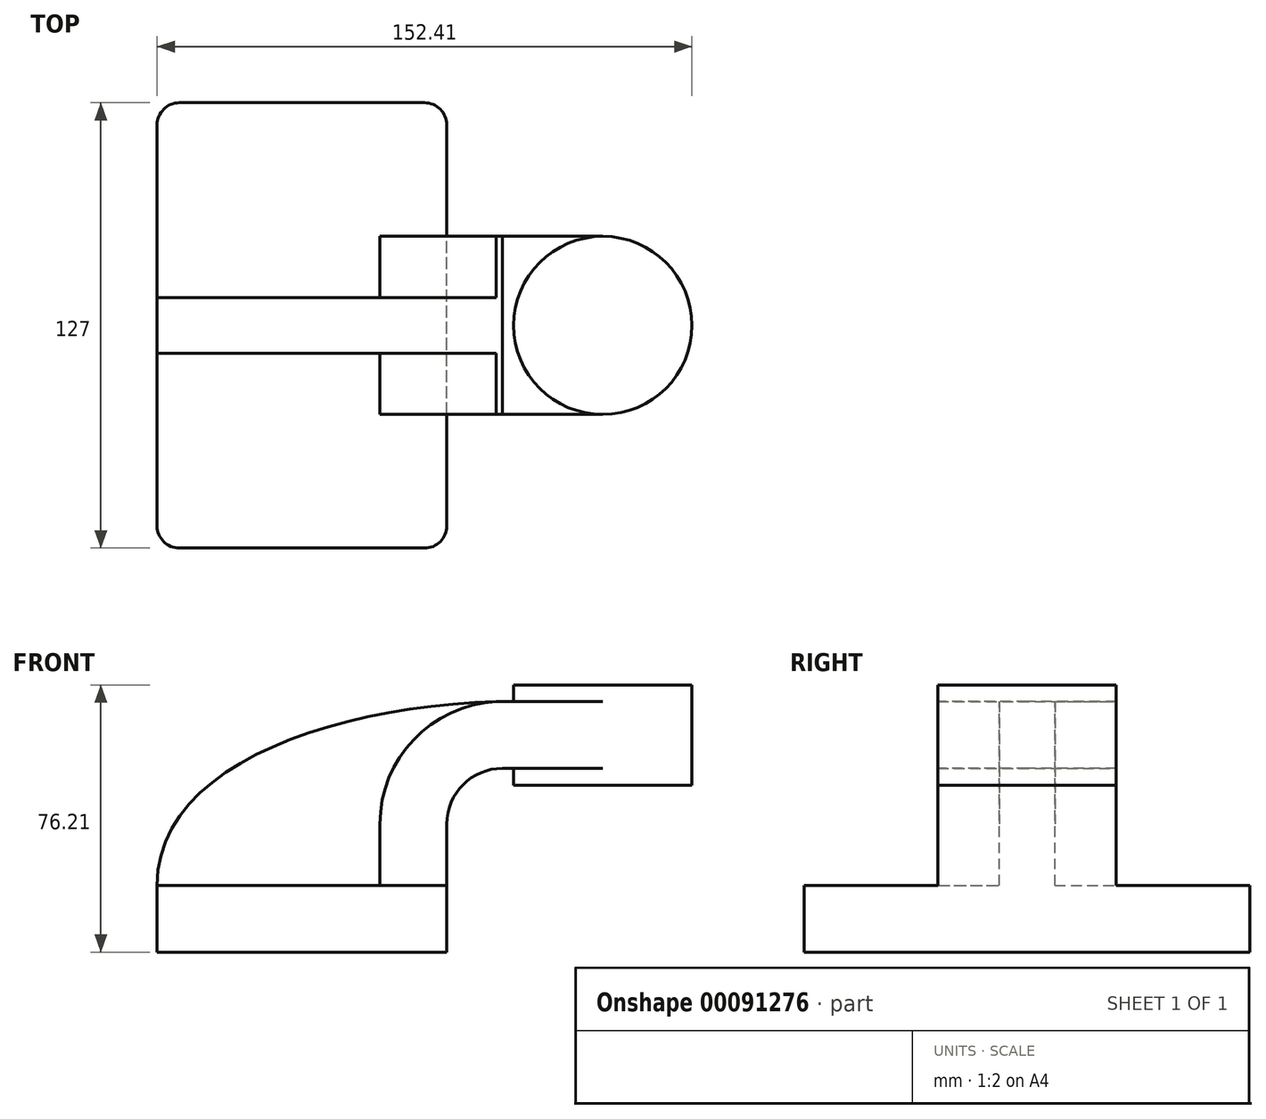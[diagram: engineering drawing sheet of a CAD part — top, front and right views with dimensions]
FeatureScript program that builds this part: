
annotation { "Feature Type Name" : "Feature", "Feature Type Description" : "" }
export const myFeature = defineFeature(function(context is Context, id is Id, definition is map)
    precondition{}
    {
        {
            var Q0;
            Q0=qCreatedBy(makeId("Front.planeOp"),FACE);
            var sketch = newSketch(context, id + "F0", { "sketchPlane" : qUnion([Q0])});
            skLineSegment(sketch, "E0.bottom", {"start": v(41.27, 9.53) * mm, "end": v(-41.28, 9.53) * mm});
            skLineSegment(sketch, "E0.top", {"start": v(41.28, -9.52) * mm, "end": v(-41.27, -9.52) * mm});
            skLineSegment(sketch, "E0.left", {"start": v(41.28, 9.53) * mm, "end": v(41.28, -9.52) * mm});
            skLineSegment(sketch, "E0.right", {"start": v(-41.28, 9.53) * mm, "end": v(-41.27, -9.52) * mm});
            skPoint(sketch, "E0.middle", {"position": v(0, 0) * mm});
            skLineSegment(sketch, "E1.bottom", {"start": v(111.13, 66.68) * mm, "end": v(60.33, 66.68) * mm});
            skLineSegment(sketch, "E1.top", {"start": v(111.13, 38.1) * mm, "end": v(60.33, 38.1) * mm});
            skLineSegment(sketch, "E1.left", {"start": v(111.13, 66.68) * mm, "end": v(111.13, 38.1) * mm});
            skLineSegment(sketch, "E1.right", {"start": v(60.33, 66.68) * mm, "end": v(60.33, 38.1) * mm});
            skPoint(sketch, "E1.middle", {"position": v(85.72, 52.39) * mm});
            skLineSegment(sketch, "E2", {"start": v(41.27, 9.53) * mm, "end": v(41.27, 27) * mm});
            skArc(sketch, "E3", {"start": v(41.27, 27) * mm, "mid": v(45.92, 38.23) * mm, "end": v(57.15, 42.88) * mm});
            skLineSegment(sketch, "E4", {"start": v(57.15, 42.88) * mm, "end": v(85.73, 42.88) * mm});
            skLineSegment(sketch, "E5.0", {"start": v(57.15, 61.93) * mm, "end": v(85.73, 61.93) * mm});
            skArc(sketch, "E5.1", {"start": v(22.23, 27) * mm, "mid": v(32.45, 51.7) * mm, "end": v(57.15, 61.93) * mm});
            skLineSegment(sketch, "E5.2", {"start": v(22.22, 9.53) * mm, "end": v(22.22, 27) * mm});
            skLineSegment(sketch, "E6", {"start": v(85.73, 38.1) * mm, "end": v(85.73, 66.68) * mm});
            skFitSpline(sketch, "E7", {"points": [v(-41.28, 9.53) * mm, v(57.15, 61.93) * mm], "startDerivative": vector(-0.3, 103.19) * mm, "endDerivative": vector(143.56, 3.08) * mm});
            skSolve(sketch);
        }
        {
            var Q0;
            Q0=makeQuery(id+"F0.imprint","IMPRINT",FACE,{"disambiguationData":[TD([[makeQuery(id+"F0.imprint","IMPRINT",EDGE,{"derivedFrom":sQuery(id+"F0.wireOp",EDGE,"E0.top")}),-1.0]])]});
            extrude(context, id + "F1", {"entities" : qUnion([Q0]), "endBound" : BoundingType.SYMMETRIC, "depth" : 127 * mm});
        }
        {
            var Q0;
            {var subQ1=sQuery(id+"F0.wireOp",EDGE,"E2");Q0=makeQuery(id+"F0.imprint","IMPRINT",FACE,{"disambiguationData":[TD([[makeQuery(id+"F0.imprint","IMPRINT",EDGE,{"derivedFrom":subQ1}),1.0]])]});}
            var Q1;
            {var subQ0=sQuery(id+"F0.wireOp",EDGE,"E5.0");var subQ1=sQuery(id+"F0.wireOp",EDGE,"E1.right");var subQ2=makeQuery(id+"F0.imprint","INTERSECT",VERTEX,{"derivedFrom":[subQ1,subQ0]});Q1=makeQuery(id+"F0.imprint","IMPRINT",FACE,{"disambiguationData":[TD([[makeQuery(id+"F0.imprint","IMPRINT",EDGE,{"disambiguationData":[TD([[subQ2,-1.0]])],"derivedFrom":subQ1}),1.0]])]});}
            extrude(context, id + "F2", {"entities" : qUnion([Q0, Q1]), "operationType" : NewBodyOperationType.ADD, "endBound" : BoundingType.SYMMETRIC, "depth" : 50.8 * mm});
        }
        {
            var Q0;
            {var subQ3=sQuery(id+"F0.wireOp",EDGE,"E5.2");Q0=makeQuery(id+"F0.imprint","IMPRINT",FACE,{"disambiguationData":[TD([[makeQuery(id+"F0.imprint","IMPRINT",EDGE,{"derivedFrom":subQ3}),1.0]])]});}
            extrude(context, id + "F3", {"entities" : qUnion([Q0]), "operationType" : NewBodyOperationType.ADD, "endBound" : BoundingType.SYMMETRIC, "depth" : 15.88 * mm});
        }
        {
            var Q0;
            {var subQ0=sQuery(id+"F0.wireOp",EDGE,"E1.left");Q0=makeQuery(id+"F0.imprint","IMPRINT",FACE,{"disambiguationData":[TD([[makeQuery(id+"F0.imprint","IMPRINT",EDGE,{"derivedFrom":subQ0}),-1.0]])]});}
            var Q1;
            Q1=sQuery(id+"F0.wireOp",EDGE,"E6");
            revolve(context, id + "F4", {"operationType" : NewBodyOperationType.ADD, "entities" : qUnion([Q0]), "axis" : qUnion([Q1]), "revolveType" : RevolveType.FULL});
        }
        {
            var Q0;
            Q0=makeQuery(id+"F1.opExtrude","CAP_EDGE",EDGE,{"disambiguationData":[OSD([sQuery(id+"F0.wireOp",EDGE,"E0.left")])],"isStart":false});
            var Q1;
            Q1=makeQuery(id+"F1.opExtrude","CAP_EDGE",EDGE,{"disambiguationData":[OSD([sQuery(id+"F0.wireOp",EDGE,"E0.right")])],"isStart":false});
            var Q2;
            Q2=makeQuery(id+"F1.opExtrude","CAP_EDGE",EDGE,{"disambiguationData":[OSD([sQuery(id+"F0.wireOp",EDGE,"E0.left")])],"isStart":true});
            var Q3;
            Q3=makeQuery(id+"F1.opExtrude","CAP_EDGE",EDGE,{"disambiguationData":[OSD([sQuery(id+"F0.wireOp",EDGE,"E0.right")])],"isStart":true});
            fillet(context, id + "F5", {"entities" : qUnion([Q0, Q1, Q2, Q3]), "radius" : 6.35 * mm, "tangentPropagation" : true, "allowEdgeOverflow" : false});
        }
    });
